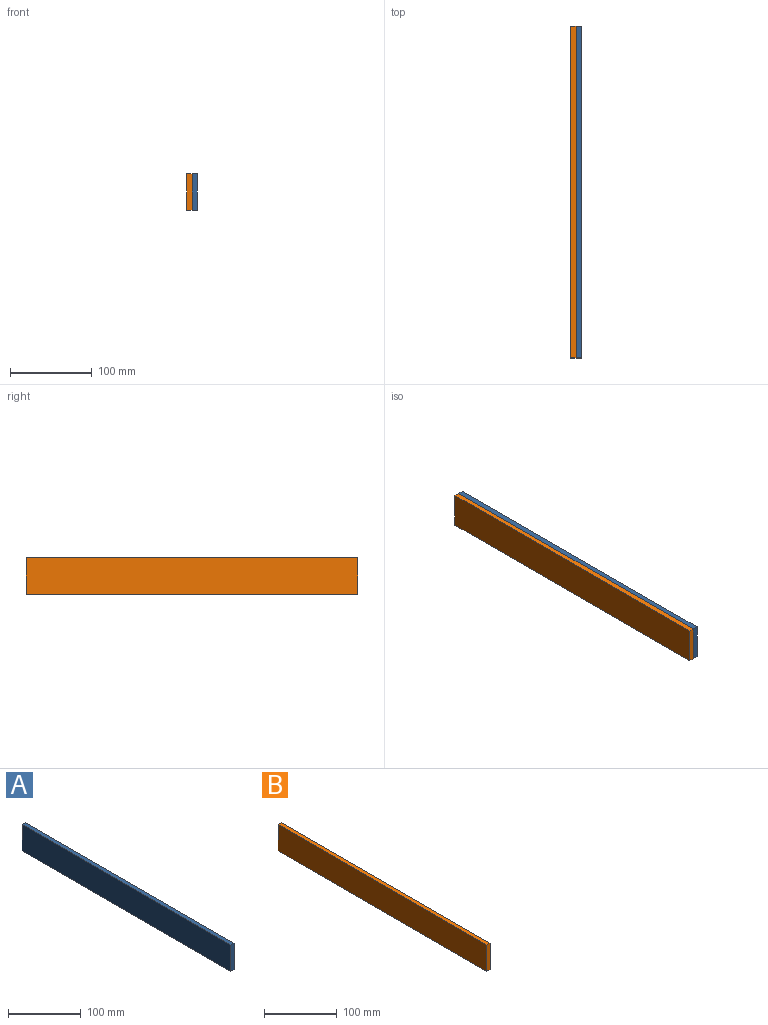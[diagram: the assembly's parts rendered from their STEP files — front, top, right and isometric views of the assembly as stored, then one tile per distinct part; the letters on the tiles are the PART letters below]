
ASSEMBLY  parts=2 mates=1
PART A: 6 faces, bbox 6.4x406.4x44.5 mm
  f0: plane 406.4x44.45mm, normal (1,0,0), area 18064.5mm2, adj f1,f3,f4,f5
  f1: plane 406.4x6.35mm, normal (0,0,1), area 2580.6mm2, adj f0,f2,f4,f5
  f2: plane 406.4x44.45mm, normal (-1,0,0), area 18064.5mm2, adj f1,f3,f4,f5
  f3: plane 406.4x6.35mm, normal (0,0,-1), area 2580.6mm2, adj f0,f2,f4,f5
  f4: plane 44.45x6.35mm, normal (0,-1,0), area 282.3mm2, adj f0,f1,f2,f3
  f5: plane 44.45x6.35mm, normal (0,1,0), area 282.3mm2, adj f0,f1,f2,f3
PART B: 6 faces, bbox 6.4x406.4x44.5 mm
  f0: plane 406.4x44.45mm, normal (1,0,0), area 18064.5mm2, adj f1,f3,f4,f5
  f1: plane 406.4x6.35mm, normal (0,0,1), area 2580.6mm2, adj f0,f2,f4,f5
  f2: plane 406.4x44.45mm, normal (-1,0,0), area 18064.5mm2, adj f1,f3,f4,f5
  f3: plane 406.4x6.35mm, normal (0,0,-1), area 2580.6mm2, adj f0,f2,f4,f5
  f4: plane 44.45x6.35mm, normal (0,-1,0), area 282.3mm2, adj f0,f1,f2,f3
  f5: plane 44.45x6.35mm, normal (0,1,0), area 282.3mm2, adj f0,f1,f2,f3
PLACE A t=(-25.4,203.2,0)mm fixed
PLACE B t=(-6.35,203.2,0)mm
MATE slider B.f4 <-> A.f4  axis (0,-1,0) through (-3.18,-203.2,22.22)mm
